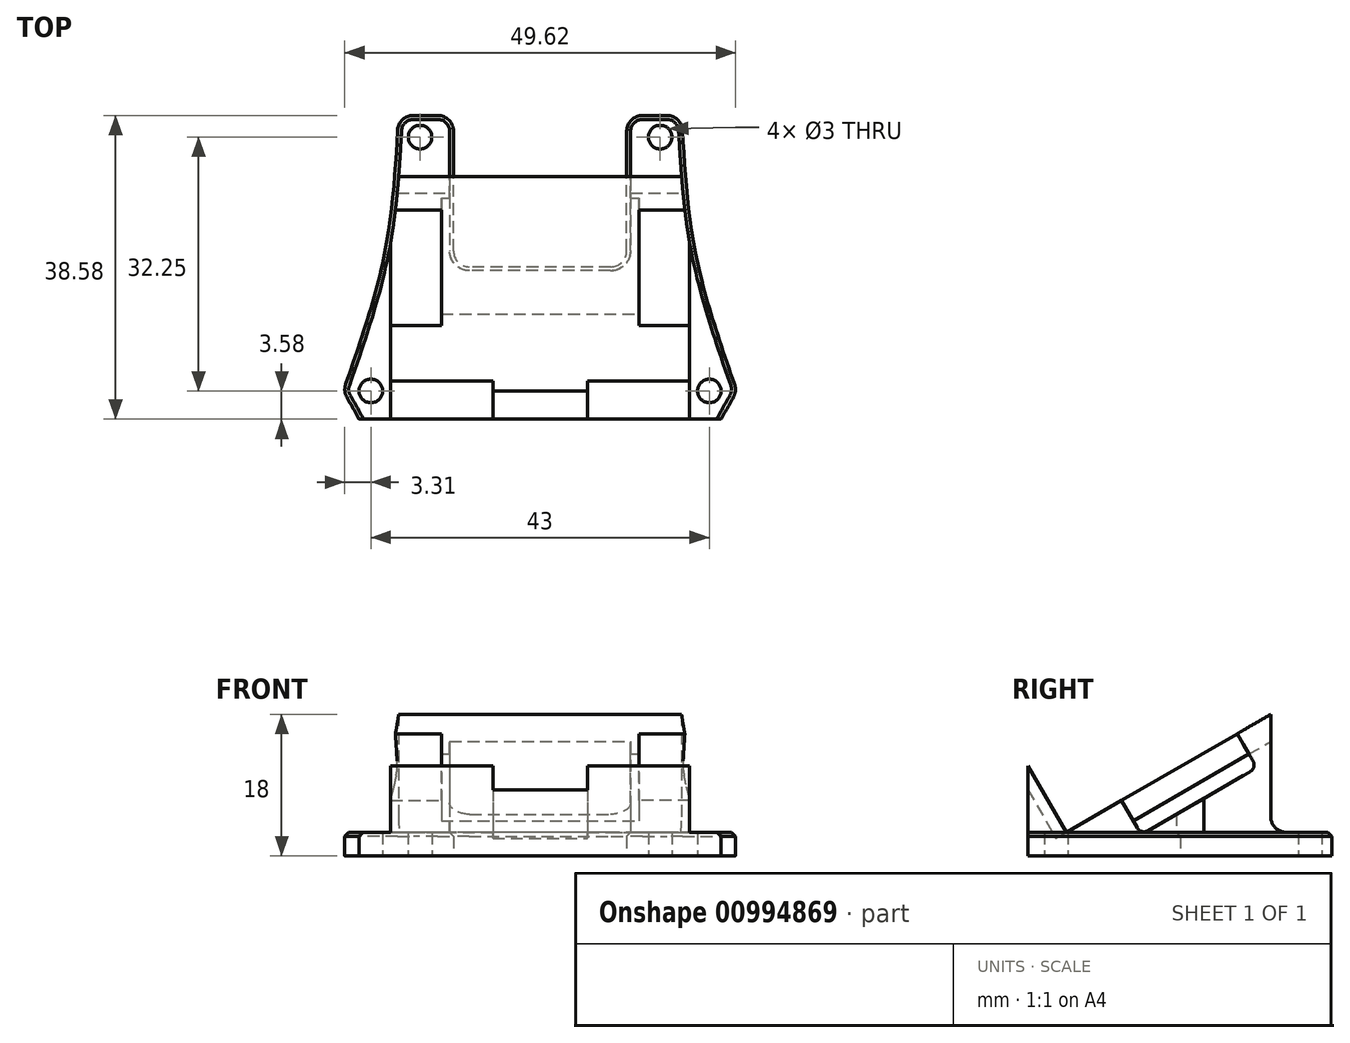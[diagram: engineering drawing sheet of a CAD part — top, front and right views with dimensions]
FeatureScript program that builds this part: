
annotation { "Feature Type Name" : "Feature", "Feature Type Description" : "" }
export const myFeature = defineFeature(function(context is Context, id is Id, definition is map)
    precondition{}
    {
        {
            var Q0;
            Q0=qCreatedBy(makeId("Top.planeOp"),FACE);
            var sketch = newSketch(context, id + "F0", { "sketchPlane" : qUnion([Q0])});
            skCircle(sketch, "E0", {"center": v(15.25, 15.25) * mm, "radius": 1.6 * mm, "construction": true});
            skCircle(sketch, "E1.MirrorC", {"center": v(-15.25, 15.25) * mm, "radius": 1.6 * mm, "construction": true});
            skCircle(sketch, "E2", {"center": v(21.5, 37) * mm, "radius": 1.5 * mm});
            skCircle(sketch, "E3", {"center": v(21.5, 37) * mm, "radius": 2.5 * mm, "construction": true});
            skCircle(sketch, "E4", {"center": v(15.25, 69.25) * mm, "radius": 1.5 * mm});
            skLineSegment(sketch, "E5.bottom", {"start": v(11, 52.77) * mm, "end": v(0, 52.77) * mm});
            skLineSegment(sketch, "E5.left", {"start": v(11, 52.77) * mm, "end": v(11, 72) * mm});
            skPoint(sketch, "E5.middle", {"position": v(0, 72) * mm});
            skLineSegment(sketch, "E6.trimOffspring", {"start": v(11, 72) * mm, "end": v(18, 72) * mm});
            skLineSegment(sketch, "E7", {"start": v(-15.25, 15.25) * mm, "end": v(-15.25, 13.65) * mm, "construction": true});
            skLineSegment(sketch, "E8", {"start": v(-15.25, 13.65) * mm, "end": v(15.25, 13.65) * mm, "construction": true});
            skLineSegment(sketch, "E9.top", {"start": v(10, 13.65) * mm, "end": v(-10, 13.65) * mm});
            skLineSegment(sketch, "E10", {"start": v(18, 72) * mm, "end": v(25, 37) * mm, "construction": true});
            skLineSegment(sketch, "E11", {"start": v(21.5, 54.5) * mm, "end": v(18, 54.5) * mm, "construction": true});
            skFitSpline(sketch, "E12", {"points": [v(18, 72) * mm, v(19.75, 54.5) * mm, v(25, 37) * mm], "startDerivative": vector(1.83, -35.5) * mm, "endDerivative": vector(12.13, -34.5) * mm});
            skLineSegment(sketch, "E13", {"start": v(-21.5, 26.13) * mm, "end": v(-18, 26.13) * mm, "construction": true});
            skFitSpline(sketch, "E14.MirrorCS", {"points": [v(25, 37) * mm, v(19.75, 26.13) * mm, v(18, 15.25) * mm], "startDerivative": vector(-11.97, -21) * mm, "endDerivative": vector(-1.95, -22.5) * mm});
            skLineSegment(sketch, "E15", {"start": v(23.08, 33.42) * mm, "end": v(0, 33.42) * mm});
            skLineSegment(sketch, "E16", {"start": v(0, 33.42) * mm, "end": v(0, 52.77) * mm});
            skSolve(sketch);
        }
        {
            var Q0;
            Q0=qSketchRegion(id+"F0",true);
            extrude(context, id + "F1", {"entities" : qUnion([Q0]), "depth" : 3 * mm, "offsetDistance" : 25 * mm});
        }
        {
            var Q0;
            Q0=makeQuery(id+"F1.opExtrude","SWEPT_EDGE",EDGE,{"disambiguationData":[OSD([sQuery(id+"F0.wireOp",EDGE,"E5.bottom"),sQuery(id+"F0.wireOp",EDGE,"E5.left")])]});
            var Q1;
            Q1=makeQuery(id+"F1.opExtrude","SWEPT_EDGE",EDGE,{"disambiguationData":[OSD([sQuery(id+"F0.wireOp",EDGE,"E5.left"),sQuery(id+"F0.wireOp",EDGE,"E6.trimOffspring")])]});
            var Q2;
            Q2=makeQuery(id+"F1.opExtrude","SWEPT_EDGE",EDGE,{"disambiguationData":[OSD([sQuery(id+"F0.wireOp",EDGE,"4EwUNQO2-gk2p-LZQ3-uuf9-EiTNVCb7oiJY.bottom"),sQuery(id+"F0.wireOp",EDGE,"E5.right")])]});
            var Q3;
            Q3=makeQuery(id+"F1.opExtrude","SWEPT_EDGE",EDGE,{"disambiguationData":[OSD([sQuery(id+"F0.wireOp",EDGE,"4EwUNQO2-gk2p-LZQ3-uuf9-EiTNVCb7oiJY.bottom"),sQuery(id+"F0.wireOp",EDGE,"4EwUNQO2-gk2p-LZQ3-uuf9-EiTNVCb7oiJY.left")])]});
            var Q4;
            Q4=makeQuery(id+"F1.opExtrude","SWEPT_EDGE",EDGE,{"disambiguationData":[OSD([sQuery(id+"F0.wireOp",EDGE,"4EwUNQO2-gk2p-LZQ3-uuf9-EiTNVCb7oiJY.right"),sQuery(id+"F0.wireOp",EDGE,"E6.trimOffspring")])]});
            var Q5;
            Q5=makeQuery(id+"F1.opExtrude","SWEPT_EDGE",EDGE,{"disambiguationData":[OSD([sQuery(id+"F0.wireOp",EDGE,"4EwUNQO2-gk2p-LZQ3-uuf9-EiTNVCb7oiJY.top"),sQuery(id+"F0.wireOp",EDGE,"4EwUNQO2-gk2p-LZQ3-uuf9-EiTNVCb7oiJY.right")])]});
            var Q6;
            Q6=makeQuery(id+"F1.opExtrude","SWEPT_EDGE",EDGE,{"disambiguationData":[OSD([sQuery(id+"F0.wireOp",EDGE,"4EwUNQO2-gk2p-LZQ3-uuf9-EiTNVCb7oiJY.top"),sQuery(id+"F0.wireOp",EDGE,"4EwUNQO2-gk2p-LZQ3-uuf9-EiTNVCb7oiJY.left")])]});
            var Q7;
            Q7=makeQuery(id+"F1.opExtrude","SWEPT_EDGE",EDGE,{"disambiguationData":[OSD([sQuery(id+"F0.wireOp",EDGE,"E9.top"),sQuery(id+"F0.wireOp",EDGE,"E9.left")])]});
            var Q8;
            Q8=makeQuery(id+"F1.opExtrude","SWEPT_EDGE",EDGE,{"disambiguationData":[OSD([sQuery(id+"F0.wireOp",EDGE,"E9.top"),sQuery(id+"F0.wireOp",EDGE,"E9.right")])]});
            var Q9;
            Q9=makeQuery(id+"F1.opExtrude","SWEPT_EDGE",EDGE,{"disambiguationData":[OSD([sQuery(id+"F0.wireOp",EDGE,"E9.bottom"),sQuery(id+"F0.wireOp",EDGE,"E9.right")])]});
            var Q10;
            Q10=makeQuery(id+"F1.opExtrude","SWEPT_EDGE",EDGE,{"disambiguationData":[OSD([sQuery(id+"F0.wireOp",EDGE,"E9.bottom"),sQuery(id+"F0.wireOp",EDGE,"E9.left")])]});
            var Q11;
            Q11=makeQuery(id+"F1.opExtrude","SWEPT_EDGE",EDGE,{"disambiguationData":[OSD([sQuery(id+"F0.wireOp",EDGE,"IwF6vI3l-43P9-IoSC-l292-cxGhL3uO0hTT.bottom"),sQuery(id+"F0.wireOp",EDGE,"IwF6vI3l-43P9-IoSC-l292-cxGhL3uO0hTT.left")])]});
            var Q12;
            Q12=makeQuery(id+"F1.opExtrude","SWEPT_EDGE",EDGE,{"disambiguationData":[OSD([sQuery(id+"F0.wireOp",EDGE,"IwF6vI3l-43P9-IoSC-l292-cxGhL3uO0hTT.bottom"),sQuery(id+"F0.wireOp",EDGE,"IwF6vI3l-43P9-IoSC-l292-cxGhL3uO0hTT.right")])]});
            var Q13;
            Q13=makeQuery(id+"F1.opExtrude","SWEPT_EDGE",EDGE,{"disambiguationData":[OSD([sQuery(id+"F0.wireOp",EDGE,"IwF6vI3l-43P9-IoSC-l292-cxGhL3uO0hTT.top"),sQuery(id+"F0.wireOp",EDGE,"IwF6vI3l-43P9-IoSC-l292-cxGhL3uO0hTT.right")])]});
            var Q14;
            Q14=makeQuery(id+"F1.opExtrude","SWEPT_EDGE",EDGE,{"disambiguationData":[OSD([sQuery(id+"F0.wireOp",EDGE,"IwF6vI3l-43P9-IoSC-l292-cxGhL3uO0hTT.top"),sQuery(id+"F0.wireOp",EDGE,"IwF6vI3l-43P9-IoSC-l292-cxGhL3uO0hTT.left")])]});
            var Q15;
            Q15=makeQuery(id+"F1.opExtrude","SWEPT_EDGE",EDGE,{"disambiguationData":[OSD([sQuery(id+"F0.wireOp",EDGE,"kCF9Iqlc-B9bQ-7PHk-ZU54-WxiFaCCjkzjI.top"),sQuery(id+"F0.wireOp",EDGE,"kCF9Iqlc-B9bQ-7PHk-ZU54-WxiFaCCjkzjI.left")])]});
            var Q16;
            Q16=makeQuery(id+"F1.opExtrude","SWEPT_EDGE",EDGE,{"disambiguationData":[OSD([sQuery(id+"F0.wireOp",EDGE,"kCF9Iqlc-B9bQ-7PHk-ZU54-WxiFaCCjkzjI.top"),sQuery(id+"F0.wireOp",EDGE,"kCF9Iqlc-B9bQ-7PHk-ZU54-WxiFaCCjkzjI.right")])]});
            var Q17;
            Q17=makeQuery(id+"F1.opExtrude","SWEPT_EDGE",EDGE,{"disambiguationData":[OSD([sQuery(id+"F0.wireOp",EDGE,"k9ro153R-0BVs-3Yrx-g3pR-jeLNpprmyCtX"),sQuery(id+"F0.wireOp",EDGE,"5JmZtMiY-QWmG-RQCH-4PEw-1wvyCTkn86x7")])]});
            var Q18;
            Q18=makeQuery(id+"F1.opExtrude","SWEPT_EDGE",EDGE,{"disambiguationData":[OSD([sQuery(id+"F0.wireOp",EDGE,"qm9y3Ypf-cbXe-6dX0-ZsD6-7xVzCvVTtMHz"),sQuery(id+"F0.wireOp",EDGE,"1ALZKmy8-mNbL-2Iju-8xiP-ry5Pkv7Yziy5")])]});
            var Q19;
            Q19=makeQuery(id+"F1.opExtrude","SWEPT_EDGE",EDGE,{"disambiguationData":[OSD([sQuery(id+"F0.wireOp",EDGE,"HJVRndbm-OSSN-JXl2-G4b4-JlD7N3VrjcjG"),sQuery(id+"F0.wireOp",EDGE,"qm9y3Ypf-cbXe-6dX0-ZsD6-7xVzCvVTtMHz")])]});
            var Q20;
            Q20=makeQuery(id+"F1.opExtrude","SWEPT_EDGE",EDGE,{"disambiguationData":[OSD([sQuery(id+"F0.wireOp",EDGE,"5JmZtMiY-QWmG-RQCH-4PEw-1wvyCTkn86x7"),sQuery(id+"F0.wireOp",EDGE,"iJKy2Y0E-vYZf-Pd8t-fcLK-D9wDMh6w1aLY")])]});
            var Q21;
            Q21=makeQuery(id+"F1.opExtrude","SWEPT_EDGE",EDGE,{"disambiguationData":[OSD([sQuery(id+"F0.wireOp",EDGE,"7ddf48ca-3a1b-4fe8-b939-8c2d3d607d9d0.MirrorCS"),sQuery(id+"F0.wireOp",EDGE,"7ddf48ca-3a1b-4fe8-b939-8c2d3d607d9d1.MirrorCS")])]});
            var Q22;
            Q22=makeQuery(id+"F1.opExtrude","SWEPT_EDGE",EDGE,{"disambiguationData":[OSD([sQuery(id+"F0.wireOp",EDGE,"79cEYJIF-AjxS-aiUu-jvyM-gJTKuYMF5cMQ"),sQuery(id+"F0.wireOp",EDGE,"uUAegvua-vEfk-1mnY-6KAw-FU2lr9x1sRSC")])]});
            var Q23;
            Q23=makeQuery(id+"F1.opExtrude","SWEPT_EDGE",EDGE,{"disambiguationData":[OSD([sQuery(id+"F0.wireOp",EDGE,"d86f913b-7f3f-44ba-90c8-39909104230e0.MirrorCS"),sQuery(id+"F0.wireOp",EDGE,"899138fa-da44-4525-97ac-77e12be3c1ef")])]});
            var Q24;
            Q24=makeQuery(id+"F1.opExtrude","SWEPT_EDGE",EDGE,{"disambiguationData":[OSD([sQuery(id+"F0.wireOp",EDGE,"E12"),sQuery(id+"F0.wireOp",EDGE,"E14.MirrorCS")])]});
            var Q25;
            Q25=makeQuery(id+"F1.opExtrude","SWEPT_EDGE",EDGE,{"disambiguationData":[OSD([sQuery(id+"F0.wireOp",EDGE,"E5.bottom"),sQuery(id+"F0.wireOp",EDGE,"E5.left")])]});
            fillet(context, id + "F2", {"entities" : qUnion([Q0, Q1, Q2, Q3, Q4, Q5, Q6, Q7, Q8, Q9, Q10, Q11, Q12, Q13, Q14, Q15, Q16, Q17, Q18, Q19, Q20, Q21, Q22, Q23, Q24, Q25]), "radius" : 2 * mm, "tangentPropagation" : true, "defaultsChanged" : false, "vertexSettings" : [], "allowEdgeOverflow" : false});
        }
        {
            var Q0;
            Q0=makeQuery(id+"F1.opExtrude","CAP_EDGE",EDGE,{"disambiguationData":[OSD([sQuery(id+"F0.wireOp",EDGE,"E5.bottom")])],"isStart":false});
            chamfer(context, id + "F3", {"entities" : qUnion([Q0]), "width" : .5 * mm, "tangentPropagation" : true});
        }
        {
            var Q0;
            Q0=makeQuery(id+"F1.opExtrude","CAP_FACE",FACE,{"disambiguationData":[OSD([sQuery(id+"F0.wireOp",EDGE,"4EwUNQO2-gk2p-LZQ3-uuf9-EiTNVCb7oiJY.bottom"),sQuery(id+"F0.wireOp",EDGE,"E2"),sQuery(id+"F0.wireOp",EDGE,"fdaef306-a1ee-41d6-a0a0-48f951c8a6c50.MirrorC"),sQuery(id+"F0.wireOp",EDGE,"E4"),sQuery(id+"F0.wireOp",EDGE,"1dae020b-8ecf-4b1f-99c1-9cd4988fb2f70.MirrorC"),sQuery(id+"F0.wireOp",EDGE,"E5.bottom"),sQuery(id+"F0.wireOp",EDGE,"E5.left"),sQuery(id+"F0.wireOp",EDGE,"E5.right"),sQuery(id+"F0.wireOp",EDGE,"E6.trimOffspring"),sQuery(id+"F0.wireOp",EDGE,"E12"),sQuery(id+"F0.wireOp",EDGE,"d86f913b-7f3f-44ba-90c8-39909104230e0.MirrorCS"),sQuery(id+"F0.wireOp",EDGE,"899138fa-da44-4525-97ac-77e12be3c1ef"),sQuery(id+"F0.wireOp",EDGE,"E14.MirrorCS"),sQuery(id+"F0.wireOp",EDGE,"E15")])],"isStart":false});
            var sketch = newSketch(context, id + "F4", { "sketchPlane" : qUnion([Q0])});
            skLineSegment(sketch, "E17", {"start": v(17.56, 72.1) * mm, "end": v(11.5, 72.1) * mm});
            skLineSegment(sketch, "E18", {"start": v(14.55, 71.5) * mm, "end": v(14.55, 66.96) * mm, "construction": true});
            skLineSegment(sketch, "E19", {"start": v(11.5, 72.1) * mm, "end": v(11.5, 52.27) * mm});
            skLineSegment(sketch, "E20", {"start": v(11.5, 52.27) * mm, "end": v(4.5, 52.27) * mm});
            skFitSpline(sketch, "E21", {"points": [v(19.7, 52.27) * mm, v(18.53, 58.84) * mm, v(17.56, 72.1) * mm], "startDerivative": vector(-5.76, 29.2) * mm, "endDerivative": vector(-1.65, 41.78) * mm});
            skLineSegment(sketch, "E22", {"start": v(19.72, 33.42) * mm, "end": v(19.7, 52.27) * mm});
            skCircle(sketch, "E23", {"center": v(21.5, 37) * mm, "radius": 2.5 * mm});
            skPoint(sketch, "E24.bottom.start.orphan", {"position": v(11.21, 33.42) * mm});
            skLineSegment(sketch, "E25", {"start": v(11.21, 33.42) * mm, "end": v(19, 33.42) * mm});
            skLineSegment(sketch, "E26", {"start": v(19, 33.42) * mm, "end": v(19, 64.78) * mm});
            skLineSegment(sketch, "E27", {"start": v(19, 33.42) * mm, "end": v(0, 33.42) * mm});
            skLineSegment(sketch, "E28", {"start": v(0, 33.42) * mm, "end": v(0, 52.27) * mm});
            skLineSegment(sketch, "E29", {"start": v(0, 52.27) * mm, "end": v(4.5, 52.27) * mm});
            skSolve(sketch);
        }
        {
            var Q0;
            Q0=makeQuery(id+"F4.imprint","IMPRINT",FACE,{"disambiguationData":[TD([[makeQuery(id+"F4.imprint","IMPRINT",EDGE,{"derivedFrom":sQuery(id+"F4.wireOp",EDGE,"E24.bottom")}),-1.0]])]});
            var Q1;
            {var subQ17=sQuery(id+"F4.wireOp",EDGE,"E25");Q1=makeQuery(id+"F4.imprint","IMPRINT",FACE,{"disambiguationData":[TD([[makeQuery(id+"F4.imprint","IMPRINT",EDGE,{"derivedFrom":subQ17}),-1.0]])]});}
            var Q2;
            {var subQ2=sQuery(id+"F4.wireOp",EDGE,"E28");Q2=makeQuery(id+"F4.imprint","IMPRINT",FACE,{"disambiguationData":[TD([[makeQuery(id+"F4.imprint","IMPRINT",EDGE,{"derivedFrom":subQ2}),-1.0]])]});}
            extrude(context, id + "F5", {"entities" : qUnion([Q0, Q1, Q2]), "operationType" : NewBodyOperationType.ADD, "depth" : 15 * mm, "offsetDistance" : 25 * mm});
        }
        {
            var Q0;
            Q0=makeQuery(id+"F5.opExtrude","SWEPT_EDGE",EDGE,{"disambiguationData":[OSD([sQuery(id+"F4.wireOp",EDGE,"9fdd42d7-ed8c-4d58-b12a-6947c5f8b7b10.MirrorCS"),sQuery(id+"F4.wireOp",EDGE,"6fddcbd6-4fa8-4cb9-8dd9-dc76465518940.MirrorCS")])]});
            var Q1;
            Q1=makeQuery(id+"F5.opExtrude","SWEPT_EDGE",EDGE,{"disambiguationData":[OSD([sQuery(id+"F4.wireOp",EDGE,"E19"),sQuery(id+"F4.wireOp",EDGE,"E20")])]});
            fillet(context, id + "F6", {"entities" : qUnion([Q0, Q1]), "tangentPropagation" : true, "radius" : 2.56 * mm, "defaultsChanged" : true, "vertexSettings" : [], "allowEdgeOverflow" : false});
        }
        {
            var Q0;
            Q0=makeQuery(id+"F5.opExtrude","SWEPT_FACE",FACE,{"disambiguationData":[OSD([sQuery(id+"F4.wireOp",EDGE,"E26")])]});
            var sketch = newSketch(context, id + "F7", { "sketchPlane" : qUnion([Q0])});
            skLineSegment(sketch, "E30", {"start": v(33.42, 3) * mm, "end": v(33.42, 22.31) * mm});
            skLineSegment(sketch, "E31", {"start": v(33.42, 3) * mm, "end": v(76.02, 3) * mm, "construction": true});
            skLineSegment(sketch, "E32", {"start": v(38.28, 3) * mm, "end": v(66.62, 19.36) * mm});
            skLineSegment(sketch, "E33", {"start": v(38.28, 3) * mm, "end": v(26.07, 24.15) * mm});
            skLineSegment(sketch, "E34", {"start": v(66.62, 19.36) * mm, "end": v(26.07, 24.15) * mm});
            skLineSegment(sketch, "E35", {"start": v(64.26, 18) * mm, "end": v(64.26, 3) * mm});
            skLineSegment(sketch, "E36", {"start": v(64.26, 3) * mm, "end": v(76.02, 3) * mm});
            skLineSegment(sketch, "E37", {"start": v(76.02, 3) * mm, "end": v(75.18, 19.65) * mm});
            skLineSegment(sketch, "E38", {"start": v(75.18, 19.65) * mm, "end": v(66.62, 19.36) * mm});
            skSolve(sketch);
        }
        {
            var Q0;
            Q0 = qSketchRegion(id + "F7", true);
            extrude(context, id + "F8", {"entities" : qUnion([Q0]), "operationType" : NewBodyOperationType.REMOVE, "oppositeDirection" : true, "depth" : 25 * mm, "offsetDistance" : 25 * mm});
        }
        {
            var Q0;
            Q0=makeQuery(id+"F1.opExtrude","SWEPT_BODY",BODY,{"disambiguationData":[OSD([sQuery(id+"F0.wireOp",EDGE,"E2"),sQuery(id+"F0.wireOp",EDGE,"E4"),sQuery(id+"F0.wireOp",EDGE,"E5.bottom"),sQuery(id+"F0.wireOp",EDGE,"E5.left"),sQuery(id+"F0.wireOp",EDGE,"E6.trimOffspring"),sQuery(id+"F0.wireOp",EDGE,"E12"),sQuery(id+"F0.wireOp",EDGE,"E14.MirrorCS"),sQuery(id+"F0.wireOp",EDGE,"E15"),sQuery(id+"F0.wireOp",EDGE,"E16")])]});
            var Q1;
            Q1=qCreatedBy(makeId("Right.planeOp"),FACE);
            mirror(context, id + "F9", {"operationType" : NewBodyOperationType.ADD, "entities" : qUnion([Q0]), "mirrorPlane" : qUnion([Q1])});
        }
        {
            var Q0;
            {var subQ0=sQuery(id+"F4.wireOp",EDGE,"E26");var subQ1=makeQuery(id+"F5.opExtrude","SWEPT_FACE",FACE,{"disambiguationData":[OSD([subQ0])]});var subQ5=sQuery(id+"F0.wireOp",EDGE,"E12");var subQ12=makeQuery(id+"F1.opExtrude","CAP_EDGE",EDGE,{"disambiguationData":[OSD([subQ5])],"isStart":false});Q0=makeQuery(id+"F8.boolean.opBoolean","SPLIT",FACE,{"disambiguationData":[TD([makeQuery(id+"F3.opChamfer","BLEND_FACE",FACE,{"disambiguationData":[OSD([subQ5]),TDD([subQ12])]})])],"derivedFrom":subQ1});}
            var sketch = newSketch(context, id + "F10", { "sketchPlane" : qUnion([Q0])});
            skLineSegment(sketch, "E39", {"start": v(53.66, 11.88) * mm, "end": v(55.16, 9.28) * mm, "construction": true});
            skLineSegment(sketch, "E40", {"start": v(55.16, 9.28) * mm, "end": v(47.66, 4.95) * mm});
            skLineSegment(sketch, "E41", {"start": v(47.66, 4.95) * mm, "end": v(48.66, 3.22) * mm});
            skLineSegment(sketch, "E42", {"start": v(48.66, 3.22) * mm, "end": v(61.65, 10.72) * mm});
            skLineSegment(sketch, "E43", {"start": v(61.65, 10.72) * mm, "end": v(60.65, 12.45) * mm});
            skLineSegment(sketch, "E44", {"start": v(55.16, 9.28) * mm, "end": v(60.65, 12.45) * mm});
            skCircle(sketch, "E45", {"center": v(61.15, 11.58) * mm, "radius": 1 * mm});
            skCircle(sketch, "E46", {"center": v(48.16, 4.08) * mm, "radius": 1 * mm});
            skLineSegment(sketch, "E47", {"start": v(61.15, 11.58) * mm, "end": v(62.01, 12.08) * mm});
            skLineSegment(sketch, "E48", {"start": v(62.01, 12.08) * mm, "end": v(61.51, 12.95) * mm});
            skLineSegment(sketch, "E49", {"start": v(60.65, 12.45) * mm, "end": v(61.51, 12.95) * mm});
            skLineSegment(sketch, "E50", {"start": v(48.16, 4.08) * mm, "end": v(47.29, 3.58) * mm});
            skLineSegment(sketch, "E51", {"start": v(47.29, 3.58) * mm, "end": v(46.79, 4.45) * mm});
            skLineSegment(sketch, "E52", {"start": v(47.66, 4.95) * mm, "end": v(46.79, 4.45) * mm});
            skSolve(sketch);
        }
        {
            var Q0;
            Q0 = qSketchRegion(id + "F10", true);
            extrude(context, id + "F11", {"entities" : qUnion([Q0]), "operationType" : NewBodyOperationType.REMOVE, "oppositeDirection" : true, "depth" : 46.8 * mm, "offsetDistance" : 25 * mm});
        }
        {
            var Q0;
            Q0=makeQuery(id+"F5.opExtrude","SWEPT_FACE",FACE,{"disambiguationData":[OSD([sQuery(id+"F4.wireOp",EDGE,"E19")])]});
            var sketch = newSketch(context, id + "F12", { "sketchPlane" : qUnion([Q0])});
            skLineSegment(sketch, "E53", {"start": v(-56.33, 9.96) * mm, "end": v(-64.26, 14.54) * mm});
            skLineSegment(sketch, "E54", {"start": v(-64.26, 14.54) * mm, "end": v(-64.26, 18) * mm});
            skLineSegment(sketch, "E55", {"start": v(-64.26, 18) * mm, "end": v(-54.83, 12.56) * mm});
            skLineSegment(sketch, "E56", {"start": v(-54.83, 12.56) * mm, "end": v(-56.33, 9.96) * mm});
            skLineSegment(sketch, "E57", {"start": v(-62.11, 11.32) * mm, "end": v(-61.26, 12.8) * mm});
            skLineSegment(sketch, "E58", {"start": v(-61.26, 12.8) * mm, "end": v(-60.3, 12.25) * mm});
            skLineSegment(sketch, "E59", {"start": v(-62.11, 11.32) * mm, "end": v(-60.3, 12.25) * mm});
            skSolve(sketch);
        }
        {
            var Q0;
            Q0=makeQuery(id+"F8.boolean.opBoolean","COPY",EDGE,{"derivedFrom":makeQuery(id+"F8.opExtrude","SWEPT_EDGE",EDGE,{"disambiguationData":[OSD([sQuery(id+"F7.wireOp",EDGE,"E35"),sQuery(id+"F7.wireOp",EDGE,"E36")])]})});
            var Q1;
            Q1=makeQuery(id+"F9.opPattern","COPY",EDGE,{"derivedFrom":makeQuery(id+"F8.boolean.opBoolean","COPY",EDGE,{"derivedFrom":makeQuery(id+"F8.opExtrude","SWEPT_EDGE",EDGE,{"disambiguationData":[OSD([sQuery(id+"F7.wireOp",EDGE,"E35"),sQuery(id+"F7.wireOp",EDGE,"E36")])]})}),"instanceName":"1"});
            fillet(context, id + "F13", {"entities" : qUnion([Q0, Q1]), "tangentPropagation" : true, "radius" : 2 * mm, "defaultsChanged" : false, "vertexSettings" : [], "allowEdgeOverflow" : false});
        }
        {
            var Q0;
            {var subQ0=makeQuery(id+"F8.boolean.opBoolean","COPY",FACE,{"derivedFrom":makeQuery(id+"F8.opExtrude","SWEPT_FACE",FACE,{"disambiguationData":[OSD([sQuery(id+"F7.wireOp",EDGE,"E33")])]})});Q0=makeQuery(id+"F9.boolean.opBoolean","MERGE",FACE,{"derivedFrom":[subQ0,makeQuery(id+"F9.opPattern","COPY",FACE,{"derivedFrom":subQ0,"instanceName":"1"})]});}
            var sketch = newSketch(context, id + "F14", { "sketchPlane" : qUnion([Q0])});
            skLineSegment(sketch, "E60", {"start": v(0, -16.54) * mm, "end": v(0, -6.82) * mm, "construction": true});
            skLineSegment(sketch, "E61.bottom", {"start": v(-6, -6.82) * mm, "end": v(6, -6.82) * mm});
            skLineSegment(sketch, "E61.top", {"start": v(-6, -16.54) * mm, "end": v(6, -16.54) * mm});
            skLineSegment(sketch, "E61.left", {"start": v(-6, -6.82) * mm, "end": v(-6, -16.54) * mm});
            skLineSegment(sketch, "E61.right", {"start": v(6, -6.82) * mm, "end": v(6, -16.54) * mm});
            skPoint(sketch, "E61.middle", {"position": v(0, -11.68) * mm});
            skSolve(sketch);
        }
        {
            var Q0;
            Q0=makeQuery(id+"F14.imprint","IMPRINT",FACE,{"disambiguationData":[TD([[makeQuery(id+"F14.imprint","IMPRINT",EDGE,{"derivedFrom":sQuery(id+"F14.wireOp",EDGE,"E61.bottom")}),-1.0]])]});
            extrude(context, id + "F15", {"entities" : qUnion([Q0]), "operationType" : NewBodyOperationType.REMOVE, "oppositeDirection" : true, "depth" : 1.5 * mm, "offsetDistance" : 25 * mm});
        }
        {
            var Q0;
            Q0=makeQuery(id+"F11.boolean.opBoolean","COPY",FACE,{"derivedFrom":makeQuery(id+"F11.opExtrude","SWEPT_FACE",FACE,{"disambiguationData":[OSD([sQuery(id+"F10.wireOp",EDGE,"E40"),sQuery(id+"F10.wireOp",EDGE,"E44"),sQuery(id+"F10.wireOp",EDGE,"E49"),sQuery(id+"F10.wireOp",EDGE,"E52")])]})});
            var sketch = newSketch(context, id + "F16", { "sketchPlane" : qUnion([Q0])});
            skLineSegment(sketch, "E62", {"start": v(18.22, -59.75) * mm, "end": v(10.61, -59.75) * mm});
            skLineSegment(sketch, "E63", {"start": v(10.61, -59.75) * mm, "end": v(10.61, -42.75) * mm});
            skLineSegment(sketch, "E64", {"start": v(10.61, -42.75) * mm, "end": v(23.3, -42.75) * mm});
            skLineSegment(sketch, "E65", {"start": v(23.3, -42.75) * mm, "end": v(23.3, -59.75) * mm});
            skLineSegment(sketch, "E66", {"start": v(23.3, -59.75) * mm, "end": v(10.61, -59.75) * mm});
            skLineSegment(sketch, "E67", {"start": v(12.53, -59.75) * mm, "end": v(12.53, -42.75) * mm});
            skLineSegment(sketch, "E68.MirrorCS", {"start": v(-10.61, -42.75) * mm, "end": v(-23.3, -42.75) * mm});
            skLineSegment(sketch, "E69.MirrorCS", {"start": v(-23.3, -42.75) * mm, "end": v(-23.3, -59.75) * mm});
            skLineSegment(sketch, "E70.MirrorCS", {"start": v(-23.3, -59.75) * mm, "end": v(-10.61, -59.75) * mm});
            skLineSegment(sketch, "E71.MirrorCS", {"start": v(-12.53, -59.75) * mm, "end": v(-12.53, -42.75) * mm});
            skLineSegment(sketch, "E72.MirrorCS", {"start": v(-18.22, -59.75) * mm, "end": v(-10.61, -59.75) * mm});
            skLineSegment(sketch, "E73", {"start": v(-18.22, -59.75) * mm, "end": v(-12.53, -59.75) * mm});
            skLineSegment(sketch, "E74", {"start": v(-12.53, -42.75) * mm, "end": v(-19, -42.75) * mm});
            skSolve(sketch);
        }
        {
            var Q0;
            {var subQ16=sQuery(id+"F16.wireOp",EDGE,"E65");Q0=makeQuery(id+"F16.imprint","IMPRINT",FACE,{"disambiguationData":[TD([[makeQuery(id+"F16.imprint","IMPRINT",EDGE,{"derivedFrom":subQ16}),-1.0]])]});}
            var Q1;
            {var subQ5=sQuery(id+"F16.wireOp",EDGE,"E67");Q1=makeQuery(id+"F16.imprint","IMPRINT",FACE,{"disambiguationData":[TD([[makeQuery(id+"F16.imprint","IMPRINT",EDGE,{"derivedFrom":subQ5}),-1.0]])]});}
            var Q2;
            {var subQ14=sQuery(id+"F16.wireOp",EDGE,"E69.MirrorCS");Q2=makeQuery(id+"F16.imprint","IMPRINT",FACE,{"disambiguationData":[TD([[makeQuery(id+"F16.imprint","IMPRINT",EDGE,{"derivedFrom":subQ14}),1.0]])]});}
            var Q3;
            Q3=makeQuery(id+"F16.imprint","IMPRINT",FACE,{"disambiguationData":[TD([[makeQuery(id+"F16.imprint","IMPRINT",EDGE,{"derivedFrom":sQuery(id+"F16.wireOp",EDGE,"E71.MirrorCS")}),1.0]])]});
            extrude(context, id + "F17", {"entities" : qUnion([Q0, Q1, Q2, Q3]), "operationType" : NewBodyOperationType.REMOVE, "endBound" : BoundingType.UP_TO_NEXT, "oppositeDirection" : true, "depth" : 25 * mm, "offsetDistance" : 25 * mm});
        }
        {
            var Q0;
            {var subQ0=sQuery(id+"F12.wireOp",EDGE,"E54");Q0=makeQuery(id+"F12.imprint","IMPRINT",FACE,{"disambiguationData":[TD([[makeQuery(id+"F12.imprint","IMPRINT",EDGE,{"derivedFrom":subQ0}),1.0]])]});}
            extrude(context, id + "F18", {"entities" : qUnion([Q0]), "operationType" : NewBodyOperationType.ADD, "endBound" : BoundingType.UP_TO_NEXT, "depth" : 25 * mm, "offsetDistance" : 25 * mm});
        }
        {
            var Q0;
            Q0=makeQuery(id+"F18.opExtrude","SWEPT_FACE",FACE,{"disambiguationData":[OSD([sQuery(id+"F12.wireOp",EDGE,"E56")])]});
            extrude(context, id + "F19", {"entities" : qUnion([Q0]), "operationType" : NewBodyOperationType.ADD, "endBound" : BoundingType.UP_TO_NEXT, "depth" : 25 * mm, "offsetDistance" : 25 * mm});
        }
    });
